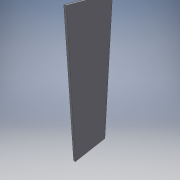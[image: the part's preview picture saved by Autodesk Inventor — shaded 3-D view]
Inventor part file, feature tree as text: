
AUTODESK INVENTOR PART (.ipt)
format: ipt  version: 2016 (Build 200138000, 138)  size: 87,552 bytes
history: native  units: in
note: dims shown in document units (in); Inventor stores cm internally (conversion verified against a paired STEP export)
features: extrude x1, sketch x1
ambient origin geometry x8: Origin, YZ Plane, XZ Plane, XY Plane, X Axis, Y Axis, Z Axis, Center Point
bodies: Solid1 (feature_tree)
feature tree (2):
  extrude  "Extrusion1"  Depth=18.0in
  sketch  "Sketch1"  dims[d0=62.0in d1=18.0in d2=1.0in d3=0.0in]
